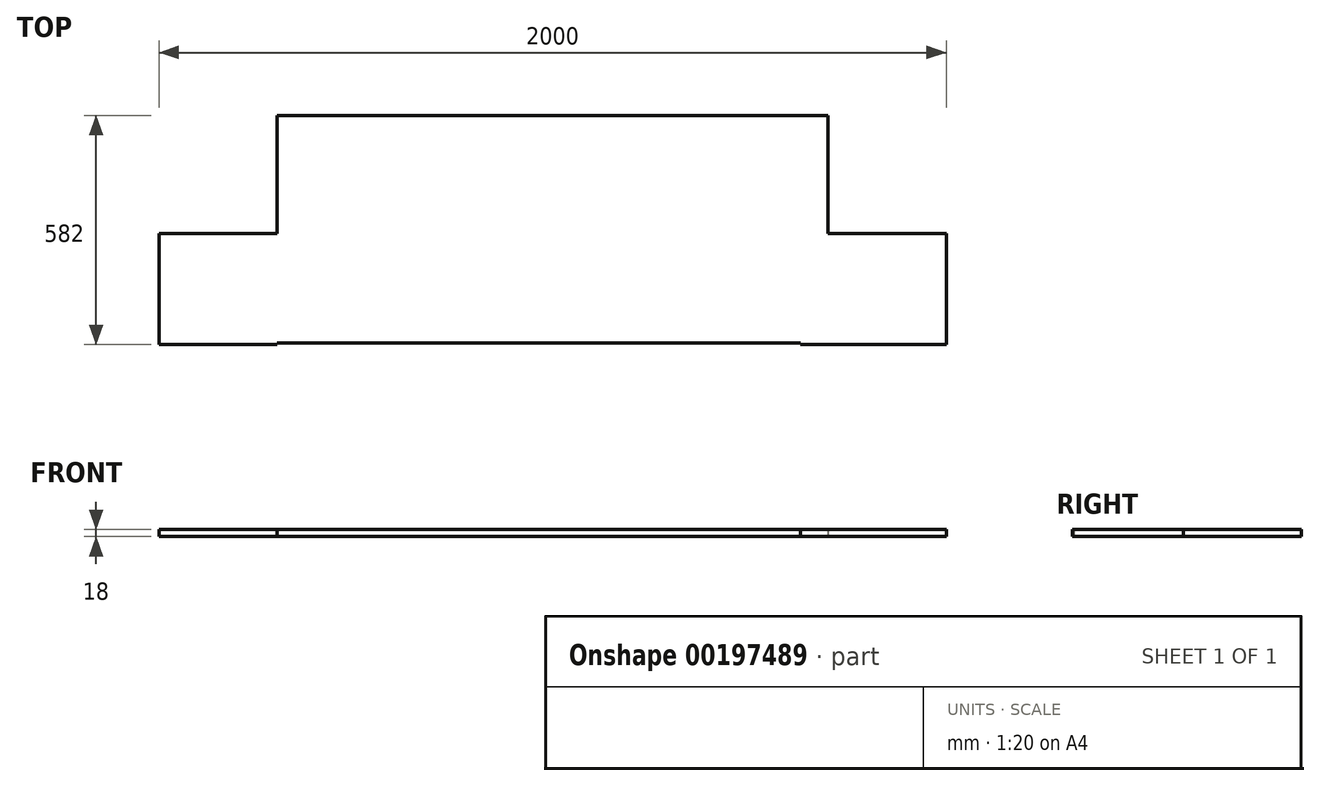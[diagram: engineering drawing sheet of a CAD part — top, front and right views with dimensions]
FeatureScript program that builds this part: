
annotation { "Feature Type Name" : "Feature", "Feature Type Description" : "" }
export const myFeature = defineFeature(function(context is Context, id is Id, definition is map)
    precondition{}
    {
        {
            var Q0;
            Q0=qCreatedBy(makeId("Top.planeOp"),FACE);
            var sketch = newSketch(context, id + "F0", { "sketchPlane" : qUnion([Q0])});
            skLineSegment(sketch, "E0.bottom", {"start": v(1000, 141) * mm, "end": v(700, 141) * mm});
            skLineSegment(sketch, "E0.top", {"start": v(1000, -141) * mm, "end": v(630, -141) * mm});
            skLineSegment(sketch, "E0.left", {"start": v(1000, 141) * mm, "end": v(1000, -141) * mm});
            skLineSegment(sketch, "E0.right", {"start": v(-1000, 141) * mm, "end": v(-1000, -141) * mm});
            skPoint(sketch, "E0.middle", {"position": v(0, 0) * mm});
            skLineSegment(sketch, "E1", {"start": v(-700, 141) * mm, "end": v(-700, 441) * mm});
            skLineSegment(sketch, "E2", {"start": v(-700, 441) * mm, "end": v(700, 441) * mm});
            skLineSegment(sketch, "E3", {"start": v(700, 441) * mm, "end": v(700, 141) * mm});
            skLineSegment(sketch, "E4.trimOffspring", {"start": v(-700, 141) * mm, "end": v(-1000, 141) * mm});
            skLineSegment(sketch, "E5", {"start": v(-700, -141) * mm, "end": v(-700, -137) * mm});
            skLineSegment(sketch, "E6", {"start": v(-700, -137) * mm, "end": v(630, -137) * mm});
            skLineSegment(sketch, "E7", {"start": v(630, -137) * mm, "end": v(630, -141) * mm});
            skLineSegment(sketch, "E8.trimOffspring", {"start": v(-700, -141) * mm, "end": v(-1000, -141) * mm});
            skSolve(sketch);
        }
        {
            var Q0;
            Q0 = qSketchRegion(id + "F0", true);
            extrude(context, id + "F1", {"entities" : qUnion([Q0]), "depth" : 18 * mm});
        }
    });
